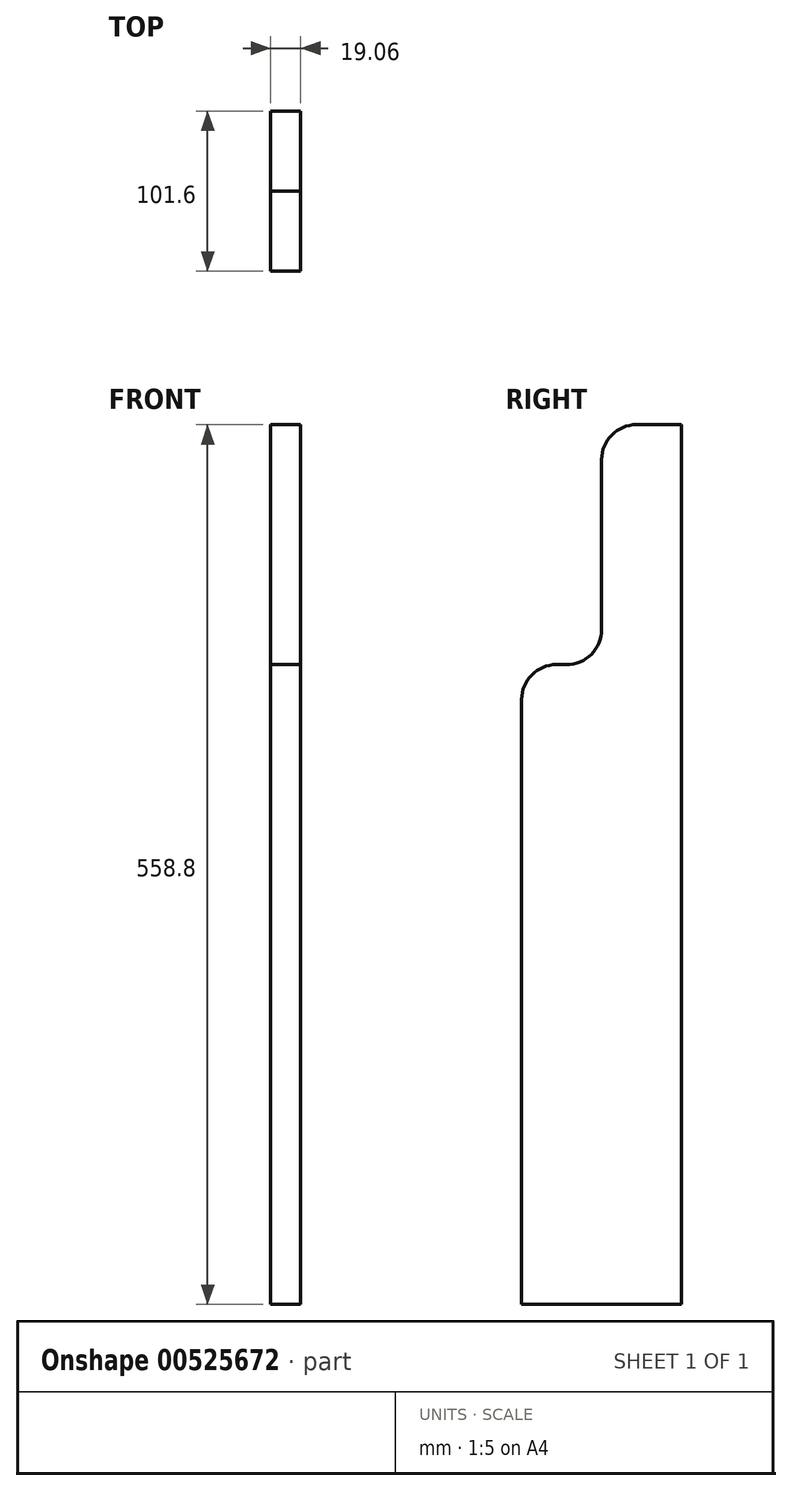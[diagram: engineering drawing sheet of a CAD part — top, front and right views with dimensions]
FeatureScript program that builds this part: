
annotation { "Feature Type Name" : "Feature", "Feature Type Description" : "" }
export const myFeature = defineFeature(function(context is Context, id is Id, definition is map)
    precondition{}
    {
        {
            var Q0;
            Q0=qCreatedBy(makeId("Right.planeOp"),FACE);
            var sketch = newSketch(context, id + "F0", { "sketchPlane" : qUnion([Q0])});
            skLineSegment(sketch, "E0", {"start": v(101.6, 355.6) * mm, "end": v(101.6, -203.2) * mm});
            skLineSegment(sketch, "E1", {"start": v(101.6, -203.2) * mm, "end": v(0, -203.2) * mm});
            skLineSegment(sketch, "E2", {"start": v(0, -203.2) * mm, "end": v(0, 203.2) * mm});
            skLineSegment(sketch, "E3", {"start": v(0, 203.2) * mm, "end": v(50.8, 203.2) * mm});
            skLineSegment(sketch, "E4", {"start": v(50.8, 203.2) * mm, "end": v(50.8, 355.6) * mm});
            skLineSegment(sketch, "E5", {"start": v(50.8, 355.6) * mm, "end": v(101.6, 355.6) * mm});
            skSolve(sketch);
        }
        {
            var Q0;
            Q0 = qSketchRegion(id + "F0", true);
            extrude(context, id + "F1", {"entities" : qUnion([Q0]), "endBound" : BoundingType.SYMMETRIC, "depth" : 19.05 * mm, "offsetDistance" : 25.4 * mm});
        }
        {
            var Q0;
            Q0=makeQuery(id+"F1.opExtrude","SWEPT_EDGE",EDGE,{"disambiguationData":[OSD([sQuery(id+"F0.wireOp",EDGE,"E4"),sQuery(id+"F0.wireOp",EDGE,"E5")])]});
            var Q1;
            Q1=makeQuery(id+"F1.opExtrude","SWEPT_EDGE",EDGE,{"disambiguationData":[OSD([sQuery(id+"F0.wireOp",EDGE,"E3"),sQuery(id+"F0.wireOp",EDGE,"E4")])]});
            var Q2;
            Q2=makeQuery(id+"F1.opExtrude","SWEPT_EDGE",EDGE,{"disambiguationData":[OSD([sQuery(id+"F0.wireOp",EDGE,"E2"),sQuery(id+"F0.wireOp",EDGE,"E3")])]});
            fillet(context, id + "F2", {"entities" : qUnion([Q0, Q1, Q2]), "radius" : 22.22 * mm, "tangentPropagation" : true, "allowEdgeOverflow" : false});
        }
    });
